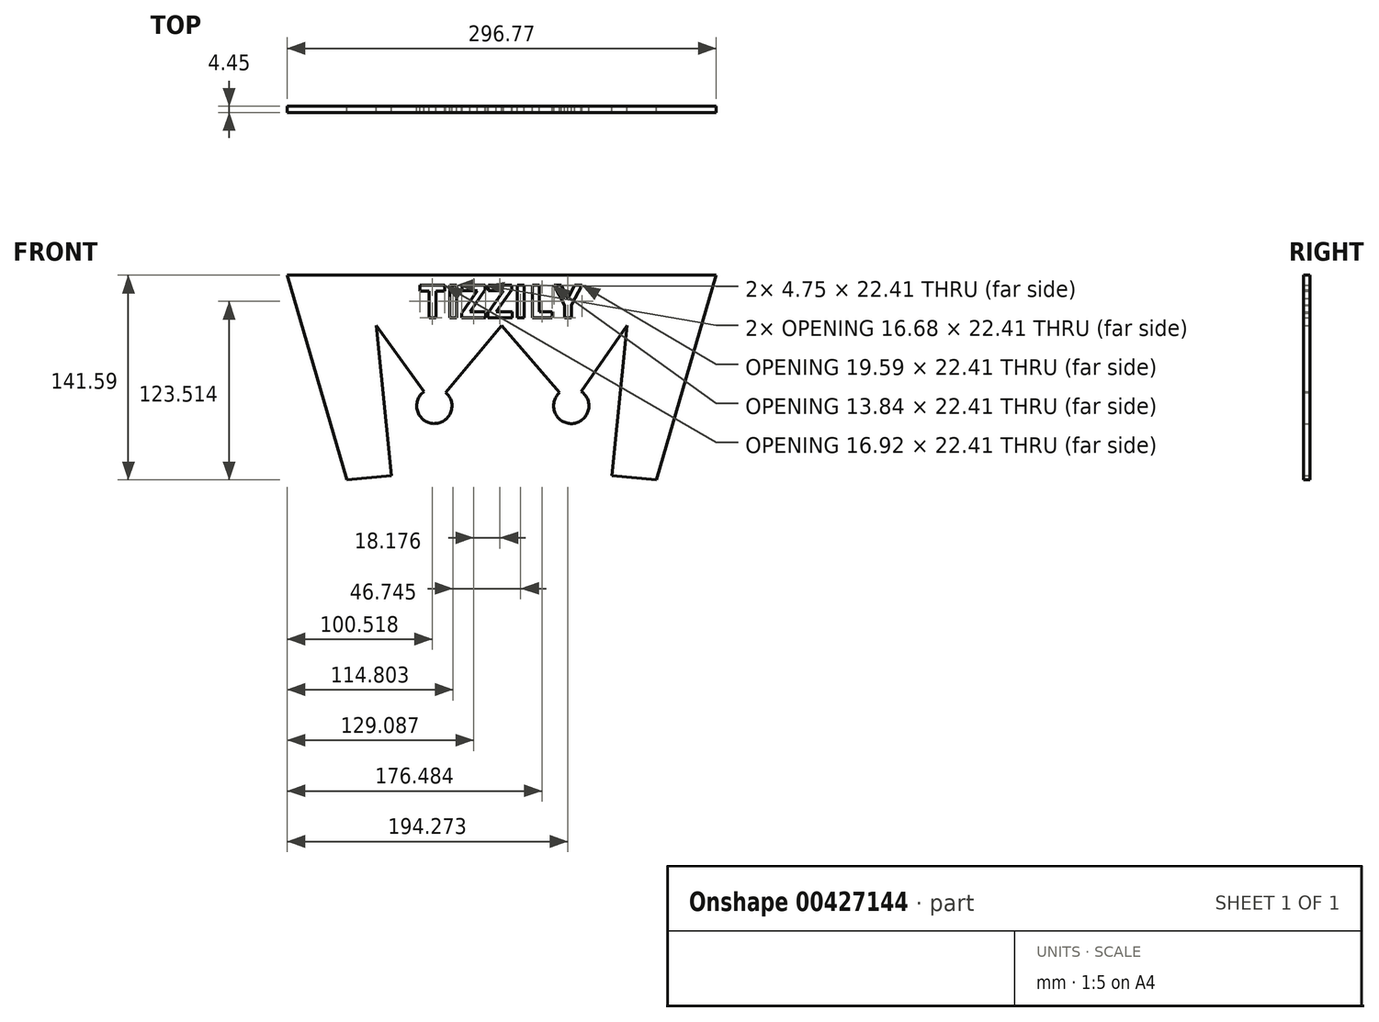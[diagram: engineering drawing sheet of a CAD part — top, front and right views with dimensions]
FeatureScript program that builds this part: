
annotation { "Feature Type Name" : "Feature", "Feature Type Description" : "" }
export const myFeature = defineFeature(function(context is Context, id is Id, definition is map)
    precondition{}
    {
        {
            var Q0;
            Q0=qCreatedBy(makeId("Front.planeOp"),FACE);
            var sketch = newSketch(context, id + "F0", { "sketchPlane" : qUnion([Q0])});
            skLineSegment(sketch, "E0", {"start": v(-76.29, 0) * mm, "end": v(76.11, 0) * mm});
            skLineSegment(sketch, "E1", {"start": v(-76.29, 0) * mm, "end": v(-86.72, 103.73) * mm});
            skLineSegment(sketch, "E2", {"start": v(-86.72, 103.73) * mm, "end": v(-46.6, 48.08) * mm});
            skLineSegment(sketch, "E3", {"start": v(-46.6, 48.08) * mm, "end": v(0, 103.73) * mm});
            skLineSegment(sketch, "E4", {"start": v(-46.6, 48.08) * mm, "end": v(48.04, 48.08) * mm});
            skLineSegment(sketch, "E5", {"start": v(0, 103.73) * mm, "end": v(48.04, 48.08) * mm});
            skCircle(sketch, "E6", {"center": v(-46.6, 48.08) * mm, "radius": 12.19 * mm});
            skCircle(sketch, "E7", {"center": v(48.04, 48.08) * mm, "radius": 12.19 * mm});
            skLineSegment(sketch, "E8", {"start": v(76.11, 0) * mm, "end": v(86.55, 103.73) * mm});
            skLineSegment(sketch, "E9", {"start": v(48.04, 48.08) * mm, "end": v(86.55, 103.73) * mm});
            skLineSegment(sketch, "E10", {"start": v(-76.29, 0) * mm, "end": v(-107.05, -3.1) * mm});
            skLineSegment(sketch, "E11", {"start": v(-107.05, -3.1) * mm, "end": v(-153.88, 156.99) * mm});
            skLineSegment(sketch, "E12", {"start": v(76.11, 0) * mm, "end": v(106.87, -3.1) * mm});
            skLineSegment(sketch, "E13", {"start": v(106.87, -3.1) * mm, "end": v(154.31, 159.06) * mm});
            skLineSegment(sketch, "E14", {"start": v(-148.47, 138.5) * mm, "end": v(148.3, 138.5) * mm});
            skText(sketch, "E15", { "text": "TIZZILY", "fontName": "OpenSans-Bold.ttf"});
            const initialGuessF0  = {"E15": [-0.05704, 0.10922, 1, 0, 0.0226]};
            skSetInitialGuess(sketch, initialGuessF0);
            skSolve(sketch);
        }
        {
            var Q0;
            {var subQ14=sQuery(id+"F0.wireOp",EDGE,"E1");Q0=makeQuery(id+"F0.imprint","IMPRINT",FACE,{"disambiguationData":[TD([[makeQuery(id+"F0.imprint","IMPRINT",EDGE,{"derivedFrom":subQ14}),1.0]])]});}
            var Q1;
            {var subQ1=sQuery(id+"F0.wireOp",EDGE,"E2");var subQ3=sQuery(id+"F0.wireOp",EDGE,"E6");var subQ4=makeQuery(id+"F0.imprint","INTERSECT",VERTEX,{"derivedFrom":[subQ1,subQ3]});Q1=makeQuery(id+"F0.imprint","IMPRINT",FACE,{"disambiguationData":[TD([[makeQuery(id+"F0.imprint","IMPRINT",EDGE,{"disambiguationData":[TD([[subQ4,-1.0]])],"derivedFrom":subQ3}),1.0]])]});}
            var Q2;
            {var subQ1=sQuery(id+"F0.wireOp",EDGE,"E2");var subQ3=sQuery(id+"F0.wireOp",EDGE,"E6");var subQ4=makeQuery(id+"F0.imprint","INTERSECT",VERTEX,{"derivedFrom":[subQ1,subQ3]});Q2=makeQuery(id+"F0.imprint","IMPRINT",FACE,{"disambiguationData":[TD([[makeQuery(id+"F0.imprint","IMPRINT",EDGE,{"disambiguationData":[TD([[subQ4,1.0]])],"derivedFrom":subQ3}),1.0]])]});}
            var Q3;
            {var subQ1=sQuery(id+"F0.wireOp",EDGE,"E3");var subQ3=sQuery(id+"F0.wireOp",EDGE,"E6");var subQ4=makeQuery(id+"F0.imprint","INTERSECT",VERTEX,{"derivedFrom":[subQ1,subQ3]});Q3=makeQuery(id+"F0.imprint","IMPRINT",FACE,{"disambiguationData":[TD([[makeQuery(id+"F0.imprint","IMPRINT",EDGE,{"disambiguationData":[TD([[subQ4,1.0]])],"derivedFrom":subQ3}),1.0]])]});}
            var Q4;
            {var subQ1=sQuery(id+"F0.wireOp",EDGE,"E4");var subQ3=sQuery(id+"F0.wireOp",EDGE,"E7");var subQ4=makeQuery(id+"F0.imprint","INTERSECT",VERTEX,{"derivedFrom":[subQ1,subQ3]});Q4=makeQuery(id+"F0.imprint","IMPRINT",FACE,{"disambiguationData":[TD([[makeQuery(id+"F0.imprint","IMPRINT",EDGE,{"disambiguationData":[TD([[subQ4,-1.0]])],"derivedFrom":subQ3}),1.0]])]});}
            var Q5;
            {var subQ1=sQuery(id+"F0.wireOp",EDGE,"E5");var subQ3=sQuery(id+"F0.wireOp",EDGE,"E7");var subQ4=makeQuery(id+"F0.imprint","INTERSECT",VERTEX,{"derivedFrom":[subQ1,subQ3]});Q5=makeQuery(id+"F0.imprint","IMPRINT",FACE,{"disambiguationData":[TD([[makeQuery(id+"F0.imprint","IMPRINT",EDGE,{"disambiguationData":[TD([[subQ4,1.0]])],"derivedFrom":subQ3}),1.0]])]});}
            var Q6;
            {var subQ1=sQuery(id+"F0.wireOp",EDGE,"E4");var subQ3=sQuery(id+"F0.wireOp",EDGE,"E7");var subQ4=makeQuery(id+"F0.imprint","INTERSECT",VERTEX,{"derivedFrom":[subQ1,subQ3]});Q6=makeQuery(id+"F0.imprint","IMPRINT",FACE,{"disambiguationData":[TD([[makeQuery(id+"F0.imprint","IMPRINT",EDGE,{"disambiguationData":[TD([[subQ4,1.0]])],"derivedFrom":subQ3}),1.0]])]});}
            extrude(context, id + "F1", {"entities" : qUnion([Q0, Q1, Q2, Q3, Q4, Q5, Q6]), "depth" : 4.44 * mm});
        }
    });
